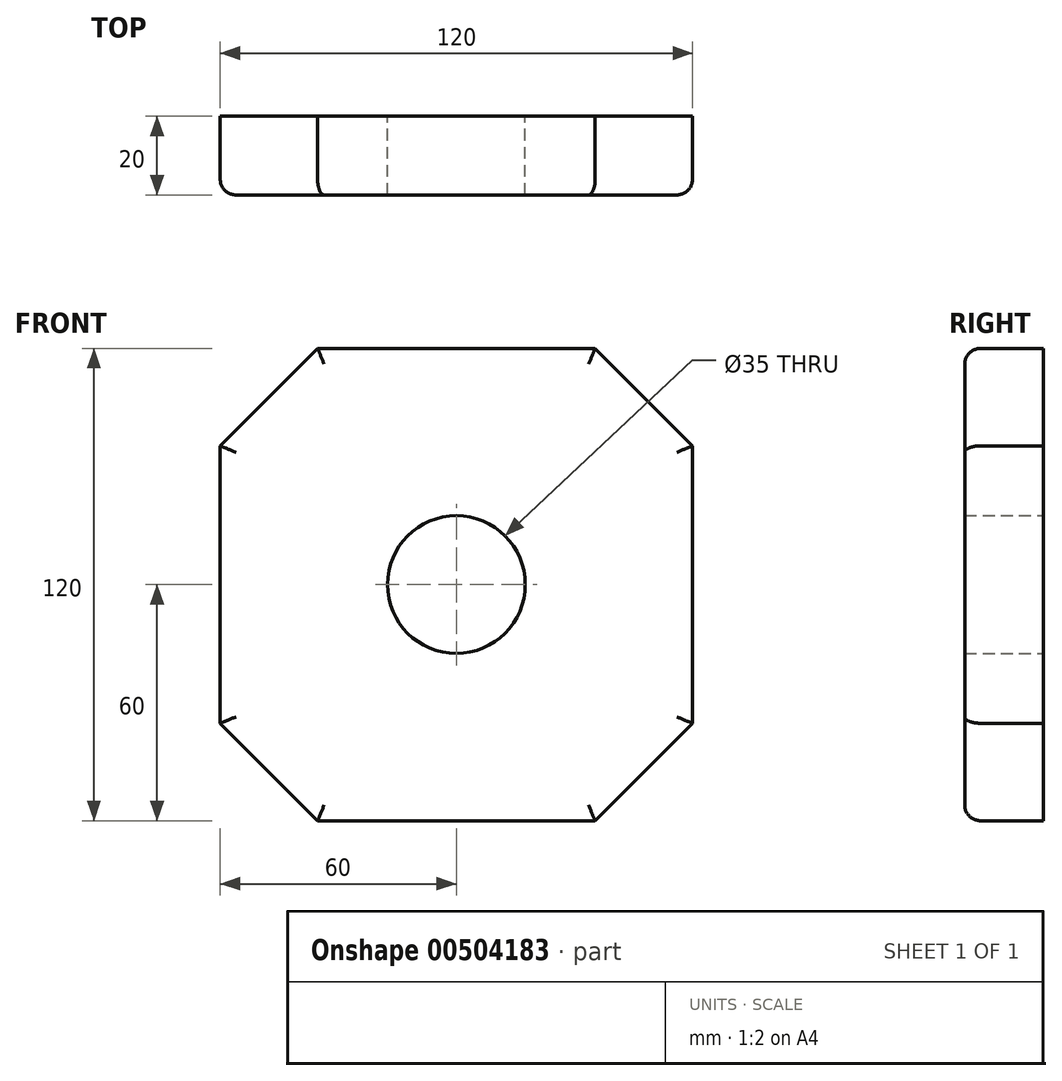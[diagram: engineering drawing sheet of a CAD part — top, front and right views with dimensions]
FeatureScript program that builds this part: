
annotation { "Feature Type Name" : "Feature", "Feature Type Description" : "" }
export const myFeature = defineFeature(function(context is Context, id is Id, definition is map)
    precondition{}
    {
        {
            var Q0;
            Q0=qCreatedBy(makeId("Front.planeOp"),FACE);
            var sketch = newSketch(context, id + "F0", { "sketchPlane" : qUnion([Q0])});
            skLineSegment(sketch, "E0.bottom", {"start": v(-35.25, 60) * mm, "end": v(35.25, 60) * mm});
            skLineSegment(sketch, "E0.top", {"start": v(-35.25, -60) * mm, "end": v(35.25, -60) * mm});
            skLineSegment(sketch, "E0.left", {"start": v(-60, 35.25) * mm, "end": v(-60, -35.25) * mm});
            skLineSegment(sketch, "E0.right", {"start": v(60, 35.25) * mm, "end": v(60, -35.25) * mm});
            skCircle(sketch, "E1", {"center": v(0, 0) * mm, "radius": 17.5 * mm});
            skLineSegment(sketch, "E2", {"start": v(-60, 35.25) * mm, "end": v(-35.25, 60) * mm});
            skLineSegment(sketch, "E3", {"start": v(-60, -35.25) * mm, "end": v(-35.25, -60) * mm});
            skLineSegment(sketch, "E4", {"start": v(35.25, -60) * mm, "end": v(60, -35.25) * mm});
            skLineSegment(sketch, "E5", {"start": v(60, 35.25) * mm, "end": v(35.25, 60) * mm});
            skSolve(sketch);
        }
        {
            var Q0;
            Q0 = qSketchRegion(id + "F0", true);
            extrude(context, id + "F1", {"entities" : qUnion([Q0]), "depth" : 20 * mm});
        }
        {
            var Q0;
            Q0=makeQuery(id+"F1.opExtrude","CAP_EDGE",EDGE,{"disambiguationData":[OSD([sQuery(id+"F0.wireOp",EDGE,"E5")])],"isStart":false});
            var Q1;
            Q1=makeQuery(id+"F1.opExtrude","CAP_EDGE",EDGE,{"disambiguationData":[OSD([sQuery(id+"F0.wireOp",EDGE,"E0.right")])],"isStart":false});
            var Q2;
            Q2=makeQuery(id+"F1.opExtrude","CAP_EDGE",EDGE,{"disambiguationData":[OSD([sQuery(id+"F0.wireOp",EDGE,"E4")])],"isStart":false});
            var Q3;
            Q3=makeQuery(id+"F1.opExtrude","CAP_EDGE",EDGE,{"disambiguationData":[OSD([sQuery(id+"F0.wireOp",EDGE,"E0.top")])],"isStart":false});
            var Q4;
            Q4=makeQuery(id+"F1.opExtrude","CAP_EDGE",EDGE,{"disambiguationData":[OSD([sQuery(id+"F0.wireOp",EDGE,"E3")])],"isStart":false});
            var Q5;
            Q5=makeQuery(id+"F1.opExtrude","CAP_EDGE",EDGE,{"disambiguationData":[OSD([sQuery(id+"F0.wireOp",EDGE,"E0.left")])],"isStart":false});
            var Q6;
            Q6=makeQuery(id+"F1.opExtrude","CAP_EDGE",EDGE,{"disambiguationData":[OSD([sQuery(id+"F0.wireOp",EDGE,"E2")])],"isStart":false});
            var Q7;
            Q7=makeQuery(id+"F1.opExtrude","CAP_EDGE",EDGE,{"disambiguationData":[OSD([sQuery(id+"F0.wireOp",EDGE,"E0.bottom")])],"isStart":false});
            fillet(context, id + "F2", {"entities" : qUnion([Q0, Q1, Q2, Q3, Q4, Q5, Q6, Q7]), "radius" : 4 * mm, "tangentPropagation" : true, "allowEdgeOverflow" : false});
        }
    });
